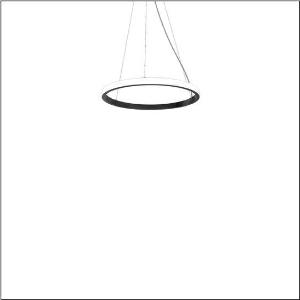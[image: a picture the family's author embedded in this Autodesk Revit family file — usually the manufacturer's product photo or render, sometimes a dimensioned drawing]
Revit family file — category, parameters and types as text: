
# Revit family: silica_r__21_ring-o_5pjbo1d3104a_0aff
name_source: partatom
category: Lighting Fixtures
units: mm (PartAtom-declared; Revit-internal decimal feet)

## family parameters
Cut with Voids When Loaded = No
Host = Face
Light Source = No
Part Type = Normal
Room Calculation Point = No
Round Connector Dimension = Use Diameter
Shared = No

## types (1)
- Silica® 21 Ring-O (1 x LED, 3930 lm, 60 W, 4000K)
    Apparent Load = 60 VA
    CIE Flux Codes = 2 16 49 50 100
    Color Rendering = 80
    Color Temperature = 4000K
    Default Elevation = 1800 mm
    Description = Silica® 21 Ring-O, suspended luminaire, of PMMA, frosted, light emission: outer ring side luminous distribution, primary light characteristic: symmetric, installation type: suspended mounting, LED, rated luminous flux: 3.930lm, luminous efficacy: 66lm/W, light colour: 840, colour temperature: 4000K, with terminal, 5-pole, mains connection: 230V, AC/DC, 0/50..60Hz, rated input power: 60W, housing, of extruded aluminium section, jet black (RAL 9005), diameter: 610mm, ceiling canopy, jet black (RAL 9005), protection rating (lamp compartment): IP40, insulation class (complete): insulation class I (protective earthing), certification: CE, impact resistance: IK02, permissible operating ambient temperature: 0..+35°C, packaging unit: 1 piece
    Height = 48 mm  [stored 0.15748 ft]
    Lamp = 1 x LED
    Lamp Light Flux = 3930 lm
    Lamp Power = 60 W
    Lamp count = 1
    Length = 610 mm
    Luminous efficacy = 66 lm/W
    Manufacturer = Siteco
    ModVariant = No
    Model = 5PJBO1D3104A
    Mounting Place = Ceiling
    Mounting Type = Pendant
    Number of Poles = 1
    OnlyDefault = Yes
    Power Factor = 1
    Product Name = Silica® 21 Ring-O
    Product group = suspended luminaire
    ProductGroupID = 904
    Protection Class = Protection class I
    Protection Degree = Degree of protection
    RLX_Detail_Level = 1
    RLX_Emergency_Light_Flux = 0 lm
    RLX_Emergency_Type = 0
    RLX_Emergency_Type_DB = No
    RlxData = <blob elided: 12149 chars, md5=d02209f3>
    Socket = socket
    Standby Power = 0 W
    System Light Flux = 3930 lm
    System Power = 60 W
    Type Comments = Product without accessories
    Type Image = l_1258377.jpg
    URL = http://relux.com
    VarID = ---
    Voltage = 0 V
    Weight = 0.00 kg
    Width = 0 mm  [stored 0 ft]

note: [stored X ft] marks values corroborated as IEEE doubles in the binary element streams (Revit-internal decimal feet)

## geometry (parser evidence)
native form markers: Sweep x14
no freeform markers — native parametric forms only
